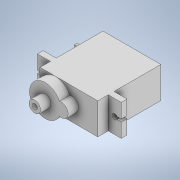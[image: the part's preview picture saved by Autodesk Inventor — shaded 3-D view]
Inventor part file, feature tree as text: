
AUTODESK INVENTOR PART (.ipt)
format: ipt  version: 2021 (Build 250183000, 183)  size: 203,776 bytes
history: native  units: mm
features: sketch x10, extrude x8, hole x2
ambient origin geometry x8: Origin, YZ Plane, XZ Plane, XY Plane, X Axis, Y Axis, Z Axis, Center Point
bodies: Solid1 (feature_tree)
feature tree (20):
  extrude  "Extrusion1"  Depth=12.0mm
  extrude  "Extrusion2"  Depth=6.0mm
  extrude  "Extrusion3"  Depth=5.0mm
  extrude  "Extrusion4"  Depth=2.2mm TaperAngle=0.0deg
  extrude  "Extrusion5"  Depth=5.0mm
  extrude  "Extrusion6"  Depth=6.0mm
  hole  "Hole1"  [1 undecoded]
  hole  "Hole2"  [1 undecoded]
  extrude  "Extrusion7"  Depth=4.0mm TaperAngle=0.0deg
  extrude  "Extrusion8"  Depth=2.5mm
  sketch  "Sketch1"  dims[d0=22.2mm d1=12.0mm]
  sketch  "Sketch2"  dims[d2=6.0mm d3=11.1mm]
  sketch  "Sketch3"  dims[d4=18.0mm d5=0.0mm d6=5.0mm]
  sketch  "Sketch4"  dims[d7=5.0mm d8=2.2mm d9=0.0mm]
  sketch  "Sketch5"  dims[d10=5.0mm d11=5.0mm]
  sketch  "Sketch6"  dims[d12=4.0mm d13=0.0mm d14=6.0mm]
  sketch  "Sketch7"  dims[d15=4.0mm d16=0.0mm d17=5.2mm]
  sketch  "Sketch8"  dims[d18=10.0mm d19=4.0mm d20=0.0mm]
  sketch  "Sketch9"  dims[d21=4.4mm d22=4.0mm d23=0.0mm]
  sketch  "Sketch10"  dims[d24=2.0mm d25=6.0mm d26=4.0mm d27=2.0mm d28=90.0deg d29=4.0mm d30=20.594885mm d31=2.5mm d32=2.5mm d33=2.0mm d34=6.0mm d35=4.0mm d36=2.0mm d37=90.0deg d38=4.0mm d39=20.594885mm d40=1.0mm d41=0.5mm d42=1.0mm d43=0.5mm d44=4.0mm d45=0.0mm d46=1.0mm d47=5.0mm d48=4.0mm d49=4.0mm d50=5.0mm d51=0.0mm]
note: 2 required parameter values undecoded (feature->parameter linkage not recoverable at this tier; creation-order binding heuristic only, values carry confidence <= 0.55)
